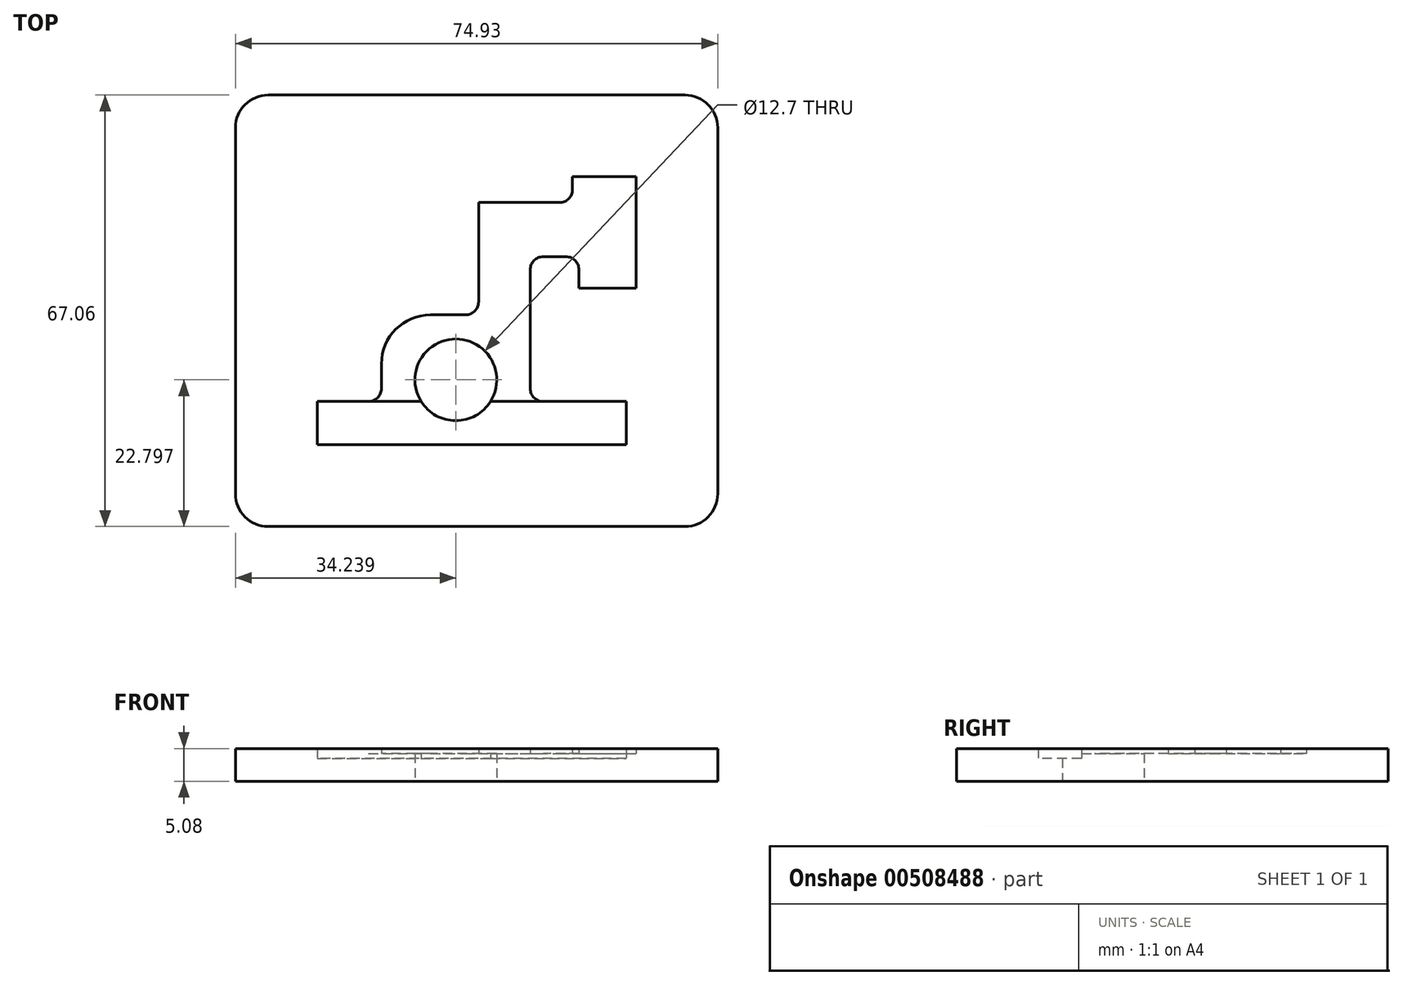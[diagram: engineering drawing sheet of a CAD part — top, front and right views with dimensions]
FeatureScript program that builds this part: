
annotation { "Feature Type Name" : "Feature", "Feature Type Description" : "" }
export const myFeature = defineFeature(function(context is Context, id is Id, definition is map)
    precondition{}
    {
        {
            var Q0;
            Q0=qCreatedBy(makeId("Top.planeOp"),FACE);
            var sketch = newSketch(context, id + "F0", { "sketchPlane" : qUnion([Q0])});
            skLineSegment(sketch, "E0", {"start": v(2.81, 41.66) * mm, "end": v(2.81, 24.3) * mm});
            skLineSegment(sketch, "E1", {"start": v(-6.05, 29.24) * mm, "end": v(-13.62, 29.24) * mm});
            skLineSegment(sketch, "E2", {"start": v(-13.62, 29.24) * mm, "end": v(-13.62, 6.73) * mm});
            skLineSegment(sketch, "E3", {"start": v(-13.62, 6.73) * mm, "end": v(1.31, 6.73) * mm});
            skLineSegment(sketch, "E4", {"start": v(1.31, 6.73) * mm, "end": v(1.31, 0) * mm});
            skLineSegment(sketch, "E5", {"start": v(1.31, 0) * mm, "end": v(-46.72, 0) * mm});
            skLineSegment(sketch, "E6", {"start": v(-46.72, 0) * mm, "end": v(-46.72, 6.73) * mm});
            skLineSegment(sketch, "E7", {"start": v(-46.72, 6.73) * mm, "end": v(-36.74, 6.73) * mm});
            skLineSegment(sketch, "E8", {"start": v(-36.74, 6.73) * mm, "end": v(-36.74, 20.2) * mm});
            skLineSegment(sketch, "E9", {"start": v(-36.74, 20.2) * mm, "end": v(-21.65, 20.2) * mm});
            skLineSegment(sketch, "E10", {"start": v(-21.65, 20.2) * mm, "end": v(-21.65, 37.64) * mm});
            skLineSegment(sketch, "E11", {"start": v(-21.65, 37.64) * mm, "end": v(-7.05, 37.64) * mm});
            skLineSegment(sketch, "E12", {"start": v(-7.05, 37.64) * mm, "end": v(-7.05, 41.66) * mm});
            skLineSegment(sketch, "E13", {"start": v(-7.05, 41.66) * mm, "end": v(2.81, 41.66) * mm});
            skLineSegment(sketch, "E14", {"start": v(-36.74, 6.73) * mm, "end": v(-13.62, 6.73) * mm});
            skLineSegment(sketch, "E15", {"start": v(-6.05, 24.3) * mm, "end": v(-6.05, 29.24) * mm});
            skLineSegment(sketch, "E16", {"start": v(-6.05, 24.3) * mm, "end": v(2.81, 24.3) * mm});
            skLineSegment(sketch, "E17.bottom", {"start": v(-59.42, 54.36) * mm, "end": v(15.51, 54.36) * mm});
            skLineSegment(sketch, "E17.top", {"start": v(-59.42, -12.7) * mm, "end": v(15.51, -12.7) * mm});
            skLineSegment(sketch, "E17.left", {"start": v(-59.42, 54.36) * mm, "end": v(-59.42, -12.7) * mm});
            skLineSegment(sketch, "E17.right", {"start": v(15.51, 54.36) * mm, "end": v(15.51, -12.7) * mm});
            skCircle(sketch, "E18", {"center": v(-25.18, 10.1) * mm, "radius": 6.35 * mm});
            skSolve(sketch);
        }
        {
            var Q0;
            Q0=makeQuery(id+"F0.imprint","IMPRINT",FACE,{"disambiguationData":[TD([[makeQuery(id+"F0.imprint","IMPRINT",EDGE,{"derivedFrom":sQuery(id+"F0.wireOp",EDGE,"E0")}),-1.0]])]});
            extrude(context, id + "F1", {"entities" : qUnion([Q0]), "depth" : 4.32 * mm});
        }
        {
            var Q0;
            Q0=makeQuery(id+"F0.imprint","IMPRINT",FACE,{"disambiguationData":[TD([[makeQuery(id+"F0.imprint","IMPRINT",EDGE,{"derivedFrom":sQuery(id+"F0.wireOp",EDGE,"E0")}),1.0]])]});
            extrude(context, id + "F2", {"entities" : qUnion([Q0]), "operationType" : NewBodyOperationType.ADD, "depth" : 5.08 * mm});
        }
        {
            var Q0;
            Q0=makeQuery(id+"F0.imprint","IMPRINT",FACE,{"disambiguationData":[TD([[makeQuery(id+"F0.imprint","IMPRINT",EDGE,{"derivedFrom":sQuery(id+"F0.wireOp",EDGE,"E3")}),-1.0]])]});
            var Q1;
            {var subQ5=sQuery(id+"F0.wireOp",EDGE,"g9WuKRJr-mzVZ-qMvp-Y0TP-tTghrKClJE1I.top");Q1=makeQuery(id+"F0.imprint","IMPRINT",FACE,{"disambiguationData":[TD([[makeQuery(id+"F0.imprint","IMPRINT",EDGE,{"derivedFrom":subQ5}),1.0]])]});}
            extrude(context, id + "F3", {"entities" : qUnion([Q0, Q1]), "operationType" : NewBodyOperationType.ADD, "depth" : 3.56 * mm});
        }
        {
            var Q0;
            Q0=makeQuery(id+"F2.opExtrude","SWEPT_EDGE",EDGE,{"disambiguationData":[OSD([sQuery(id+"F0.wireOp",EDGE,"E11"),sQuery(id+"F0.wireOp",EDGE,"E12")])]});
            var Q1;
            Q1=makeQuery(id+"F2.opExtrude","SWEPT_EDGE",EDGE,{"disambiguationData":[OSD([sQuery(id+"F0.wireOp",EDGE,"6aZ43ACk-VP0D-n7C8-ltv8-q2j5NP5bt8VM"),sQuery(id+"F0.wireOp",EDGE,"E1")])]});
            var Q2;
            Q2=makeQuery(id+"F2.opExtrude","SWEPT_EDGE",EDGE,{"disambiguationData":[OSD([sQuery(id+"F0.wireOp",EDGE,"E1"),sQuery(id+"F0.wireOp",EDGE,"E2")])]});
            var Q3;
            Q3=makeQuery(id+"F2.opExtrude","SWEPT_EDGE",EDGE,{"disambiguationData":[OSD([sQuery(id+"F0.wireOp",EDGE,"E9"),sQuery(id+"F0.wireOp",EDGE,"E10")])]});
            var Q4;
            Q4=makeQuery(id+"F2.opExtrude","SWEPT_EDGE",EDGE,{"disambiguationData":[OSD([sQuery(id+"F0.wireOp",EDGE,"E2"),sQuery(id+"F0.wireOp",EDGE,"E3")])]});
            var Q5;
            Q5=makeQuery(id+"F2.opExtrude","SWEPT_EDGE",EDGE,{"disambiguationData":[OSD([sQuery(id+"F0.wireOp",EDGE,"E7"),sQuery(id+"F0.wireOp",EDGE,"E8")])]});
            fillet(context, id + "F4", {"entities" : qUnion([Q0, Q1, Q2, Q3, Q4, Q5]), "radius" : 2.03 * mm, "tangentPropagation" : true, "allowEdgeOverflow" : false});
        }
        {
            var Q0;
            Q0=makeQuery(id+"F2.opExtrude","SWEPT_EDGE",EDGE,{"disambiguationData":[OSD([sQuery(id+"F0.wireOp",EDGE,"E8"),sQuery(id+"F0.wireOp",EDGE,"E9")])]});
            fillet(context, id + "F5", {"entities" : qUnion([Q0]), "radius" : 7.62 * mm, "tangentPropagation" : true, "allowEdgeOverflow" : false});
        }
        {
            var Q0;
            Q0=makeQuery(id+"F2.opExtrude","SWEPT_EDGE",EDGE,{"disambiguationData":[OSD([sQuery(id+"F0.wireOp",EDGE,"E17.top"),sQuery(id+"F0.wireOp",EDGE,"E17.right")])]});
            var Q1;
            Q1=makeQuery(id+"F2.opExtrude","SWEPT_EDGE",EDGE,{"disambiguationData":[OSD([sQuery(id+"F0.wireOp",EDGE,"E17.bottom"),sQuery(id+"F0.wireOp",EDGE,"E17.right")])]});
            var Q2;
            Q2=makeQuery(id+"F2.opExtrude","SWEPT_EDGE",EDGE,{"disambiguationData":[OSD([sQuery(id+"F0.wireOp",EDGE,"E17.bottom"),sQuery(id+"F0.wireOp",EDGE,"E17.left")])]});
            var Q3;
            Q3=makeQuery(id+"F2.opExtrude","SWEPT_EDGE",EDGE,{"disambiguationData":[OSD([sQuery(id+"F0.wireOp",EDGE,"E17.top"),sQuery(id+"F0.wireOp",EDGE,"E17.left")])]});
            fillet(context, id + "F6", {"entities" : qUnion([Q0, Q1, Q2, Q3]), "radius" : 5.08 * mm, "tangentPropagation" : true, "allowEdgeOverflow" : false});
        }
    });
